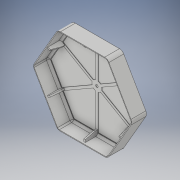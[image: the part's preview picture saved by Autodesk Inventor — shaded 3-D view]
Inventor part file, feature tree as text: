
AUTODESK INVENTOR PART (.ipt)
format: ipt  version: 2019 (Build 230136000, 136)  size: 321,024 bytes
history: native  units: mm
features: sketch x8, extrude x5, mirror x4, projected_geometry x4, plane x3, fillet x3, other x3, shell x1, pattern_circular x1
ambient origin geometry x8: Origin, YZ Plane, XZ Plane, XY Plane, X Axis, Y Axis, Z Axis, Center Point
bodies: Solid1 (feature_tree)
feature tree (32):
  extrude  "Extrusion1"  Depth=30.0mm TaperAngle=0.0deg
  shell  "Shell1"  Thickness=1.5mm
  sketch  "Sketch2"  dims[d5=2.0mm d6=15.0mm]
  plane  "Work Plane1"
  plane  "Work Plane2"
  plane  "Work Plane3"
  extrude  "Extrusion5"  Depth=2.0mm
  extrude  "Extrusion2"  Depth=1.0mm TaperAngle=0.0deg
  mirror  "Mirror1"
  mirror  "Mirror2"
  mirror  "Mirror3"
  mirror  "Mirror4"
  extrude  "Extrusion6"  Depth=10.0mm
  extrude  "Extrusion8"  Depth=5.0mm
  pattern_circular  "Circular Pattern1"  Angle=90.0deg  [1 undecoded]
  fillet  "Fillet1"  Radius=5.5mm
  fillet  "Fillet2"  Radius=0.75mm
  fillet  "Fillet4"  Radius=5.0mm
  sketch  "Sketch5"  dims[d10=4.0mm d11=10.0mm]
  sketch  "Sketch6"  dims[d12=1.0mm d37=5.0mm]
  sketch  "Sketch7"  dims[d44=10.0mm]
  other  "Work Axis4"
  other  "Work Axis5"
  other  "Work Axis6"
  sketch  "Sketch1"  dims[d0=175.0mm d2=30.0mm d3=0.0mm d4=1.5mm]
  projected_geometry  "Projected Loop1"
  sketch  "Sketch4"  dims[d7=15.0mm d8=1.0mm d9=0.0mm]
  projected_geometry  "Projected Loop3"
  sketch  "Sketch8"  dims[d45=60.0deg]
  projected_geometry  "Projected Loop4"
  sketch  "Sketch9"  dims[d46=90.0deg d47=90.0deg d52=5.5mm d53=0.75mm d54=0.0mm d55=5.0mm d56=2.0mm d57=3.0mm d58=10.0mm d59=25.0mm d60=0.0mm d70=60.0mm d72=360.0deg d74=60.0mm d75=360.0deg d77=5.0mm d78=20.0mm d79=20.0mm d80=0.0mm]
  projected_geometry  "Projected Loop5"
note: 1 required parameter value undecoded (feature->parameter linkage not recoverable at this tier; creation-order binding heuristic only, values carry confidence <= 0.55)
